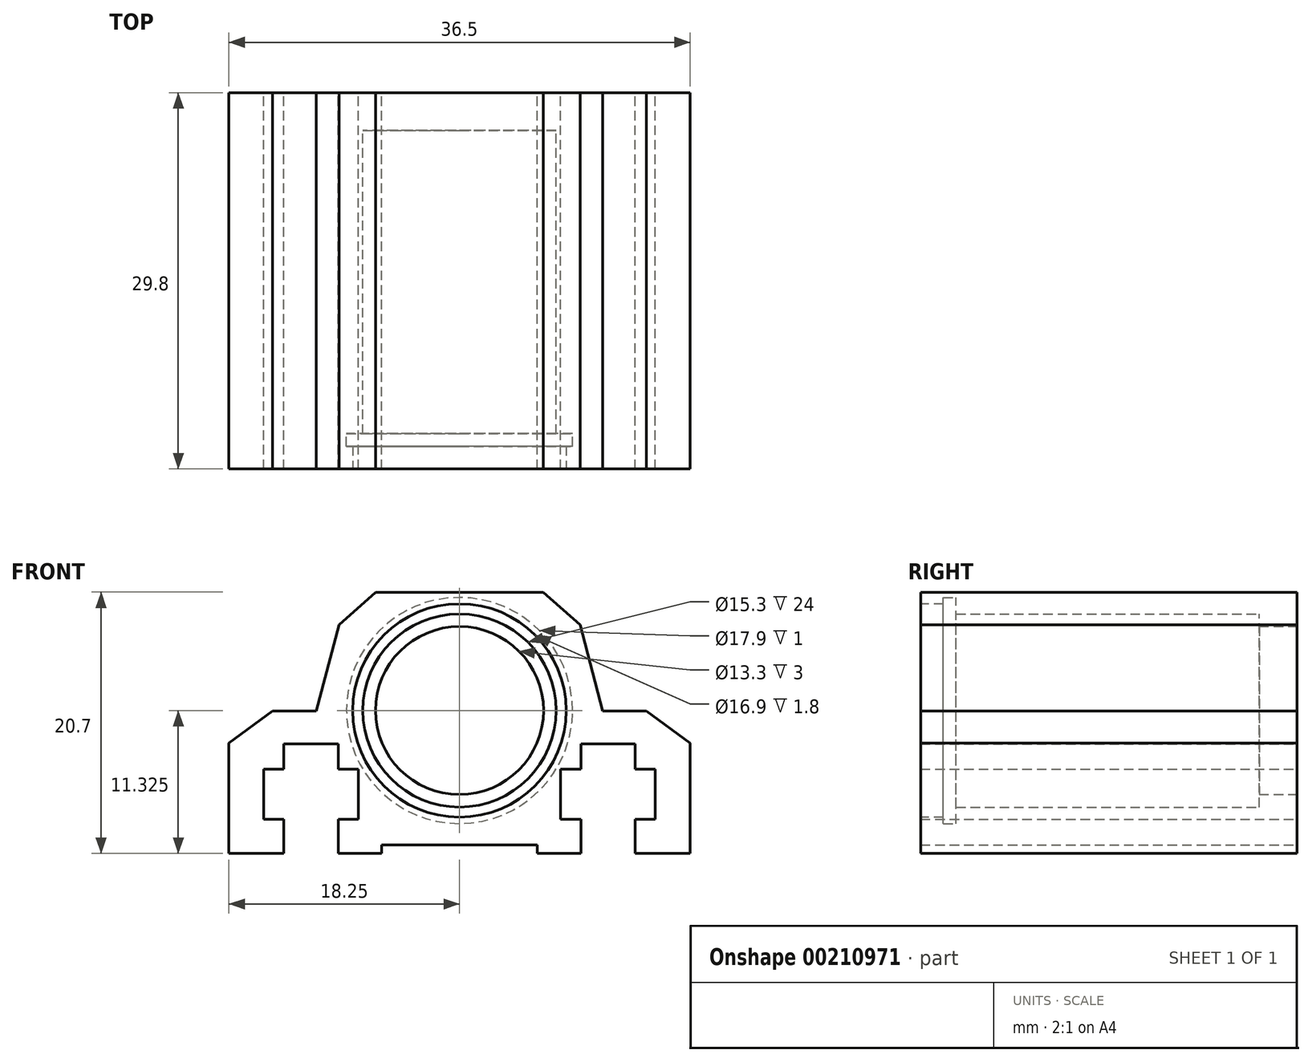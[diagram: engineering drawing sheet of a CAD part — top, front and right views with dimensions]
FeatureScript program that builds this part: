
annotation { "Feature Type Name" : "Feature", "Feature Type Description" : "" }
export const myFeature = defineFeature(function(context is Context, id is Id, definition is map)
    precondition{}
    {
        {
            var Q0;
            Q0=qCreatedBy(makeId("Front.planeOp"),FACE);
            var sketch = newSketch(context, id + "F0", { "sketchPlane" : qUnion([Q0])});
            skLineSegment(sketch, "E0", {"start": v(0, 0) * mm, "end": v(0, 26.85) * mm, "construction": true});
            skLineSegment(sketch, "E1", {"start": v(6.16, 0) * mm, "end": v(9.6, 0) * mm});
            skLineSegment(sketch, "E2", {"start": v(9.6, 0) * mm, "end": v(9.6, 2.7) * mm});
            skLineSegment(sketch, "E3", {"start": v(9.6, 2.7) * mm, "end": v(8, 2.7) * mm});
            skLineSegment(sketch, "E4", {"start": v(8, 2.7) * mm, "end": v(8, 6.7) * mm});
            skLineSegment(sketch, "E5", {"start": v(8, 6.7) * mm, "end": v(9.6, 6.7) * mm});
            skLineSegment(sketch, "E6", {"start": v(15.5, 6.7) * mm, "end": v(15.5, 2.7) * mm});
            skLineSegment(sketch, "E7", {"start": v(15.5, 2.7) * mm, "end": v(13.9, 2.7) * mm});
            skLineSegment(sketch, "E8", {"start": v(13.9, 2.7) * mm, "end": v(13.9, 0) * mm});
            skLineSegment(sketch, "E9", {"start": v(13.9, 0) * mm, "end": v(18.25, 0) * mm});
            skLineSegment(sketch, "E10", {"start": v(18.25, 0) * mm, "end": v(18.25, 8.74) * mm});
            skLineSegment(sketch, "E11", {"start": v(14.8, 11.3) * mm, "end": v(11.33, 11.3) * mm});
            skLineSegment(sketch, "E12", {"start": v(13.9, 6.7) * mm, "end": v(13.9, 8.67) * mm});
            skLineSegment(sketch, "E13", {"start": v(13.9, 8.67) * mm, "end": v(9.6, 8.67) * mm});
            skLineSegment(sketch, "E14", {"start": v(9.6, 8.67) * mm, "end": v(9.6, 6.7) * mm});
            skLineSegment(sketch, "E15.trimOffspring", {"start": v(13.9, 6.7) * mm, "end": v(15.5, 6.7) * mm});
            skLineSegment(sketch, "E16", {"start": v(6.16, 0) * mm, "end": v(6.16, 0.68) * mm});
            skLineSegment(sketch, "E17", {"start": v(6.16, 0.68) * mm, "end": v(0, 0.68) * mm});
            skCircle(sketch, "E18", {"center": v(0, 11.33) * mm, "radius": 7.65 * mm});
            skLineSegment(sketch, "E19", {"start": v(11.33, 11.3) * mm, "end": v(9.54, 18.1) * mm});
            skLineSegment(sketch, "E20", {"start": v(6.64, 20.7) * mm, "end": v(0, 20.7) * mm});
            skLineSegment(sketch, "E21.MirrorCS", {"start": v(-13.9, 6.7) * mm, "end": v(-15.5, 6.7) * mm});
            skLineSegment(sketch, "E22.MirrorCS", {"start": v(-9.6, 8.67) * mm, "end": v(-9.6, 6.7) * mm});
            skLineSegment(sketch, "E23.MirrorCS", {"start": v(-6.16, 0) * mm, "end": v(-6.16, 0.68) * mm});
            skLineSegment(sketch, "E24.MirrorCS", {"start": v(-13.9, 6.7) * mm, "end": v(-13.9, 8.67) * mm});
            skLineSegment(sketch, "E25.MirrorCS", {"start": v(-9.6, 2.7) * mm, "end": v(-8, 2.7) * mm});
            skLineSegment(sketch, "E26.MirrorCS", {"start": v(-15.5, 2.7) * mm, "end": v(-13.9, 2.7) * mm});
            skLineSegment(sketch, "E27.MirrorCS", {"start": v(-8, 6.7) * mm, "end": v(-9.6, 6.7) * mm});
            skLineSegment(sketch, "E28.MirrorCS", {"start": v(-6.16, 0) * mm, "end": v(-9.6, 0) * mm});
            skLineSegment(sketch, "E29.MirrorCS", {"start": v(-13.9, 8.67) * mm, "end": v(-9.6, 8.67) * mm});
            skLineSegment(sketch, "E30.MirrorCS", {"start": v(-9.6, 0) * mm, "end": v(-9.6, 2.7) * mm});
            skLineSegment(sketch, "E31.MirrorCS", {"start": v(-11.33, 11.3) * mm, "end": v(-9.54, 18.1) * mm});
            skLineSegment(sketch, "E32.MirrorCS", {"start": v(-18.25, 0) * mm, "end": v(-18.25, 8.74) * mm});
            skLineSegment(sketch, "E33.MirrorCS", {"start": v(-13.9, 0) * mm, "end": v(-18.25, 0) * mm});
            skLineSegment(sketch, "E34.MirrorCS", {"start": v(-6.64, 20.7) * mm, "end": v(0, 20.7) * mm});
            skLineSegment(sketch, "E35.MirrorCS", {"start": v(-14.8, 11.3) * mm, "end": v(-11.33, 11.3) * mm});
            skLineSegment(sketch, "E36.MirrorCS", {"start": v(-6.16, 0.68) * mm, "end": v(0, 0.68) * mm});
            skLineSegment(sketch, "E37.MirrorCS", {"start": v(-13.9, 2.7) * mm, "end": v(-13.9, 0) * mm});
            skLineSegment(sketch, "E38.MirrorCS", {"start": v(-8, 2.7) * mm, "end": v(-8, 6.7) * mm});
            skLineSegment(sketch, "E39.MirrorCS", {"start": v(-15.5, 6.7) * mm, "end": v(-15.5, 2.7) * mm});
            skLineSegment(sketch, "E40", {"start": v(18.25, 8.74) * mm, "end": v(14.8, 11.3) * mm});
            skLineSegment(sketch, "E41", {"start": v(9.54, 18.1) * mm, "end": v(6.64, 20.7) * mm});
            skPoint(sketch, "E42.orphan", {"position": v(8.85, 20.7) * mm});
            skPoint(sketch, "E43.orphan", {"position": v(18.25, 11.3) * mm});
            skLineSegment(sketch, "E44.MirrorCS", {"start": v(-9.54, 18.1) * mm, "end": v(-6.64, 20.7) * mm});
            skLineSegment(sketch, "E45.MirrorCS", {"start": v(-18.25, 8.74) * mm, "end": v(-14.8, 11.3) * mm});
            skPoint(sketch, "E46.orphan", {"position": v(-8.85, 20.7) * mm});
            skPoint(sketch, "E47.orphan", {"position": v(-18.25, 11.3) * mm});
            skSolve(sketch);
        }
        {
            var Q0;
            Q0=makeQuery(id+"F0.imprint","IMPRINT",FACE,{"disambiguationData":[TD([[makeQuery(id+"F0.imprint","IMPRINT",EDGE,{"derivedFrom":sQuery(id+"F0.wireOp",EDGE,"E1")}),1.0]])]});
            extrude(context, id + "F1", {"entities" : qUnion([Q0]), "endBound" : BoundingType.SYMMETRIC, "depth" : (23.8 + 6) * mm});
        }
        {
            var Q0;
            Q0=makeQuery(id+"F1.opExtrude","CAP_FACE",FACE,{"disambiguationData":[OSD([sQuery(id+"F0.wireOp",EDGE,"E1"),sQuery(id+"F0.wireOp",EDGE,"E2"),sQuery(id+"F0.wireOp",EDGE,"E3"),sQuery(id+"F0.wireOp",EDGE,"E4"),sQuery(id+"F0.wireOp",EDGE,"E5"),sQuery(id+"F0.wireOp",EDGE,"E6"),sQuery(id+"F0.wireOp",EDGE,"E7"),sQuery(id+"F0.wireOp",EDGE,"E8"),sQuery(id+"F0.wireOp",EDGE,"E9"),sQuery(id+"F0.wireOp",EDGE,"E10"),sQuery(id+"F0.wireOp",EDGE,"E11"),sQuery(id+"F0.wireOp",EDGE,"E12"),sQuery(id+"F0.wireOp",EDGE,"E13"),sQuery(id+"F0.wireOp",EDGE,"E14"),sQuery(id+"F0.wireOp",EDGE,"E15.trimOffspring"),sQuery(id+"F0.wireOp",EDGE,"E16"),sQuery(id+"F0.wireOp",EDGE,"E17"),sQuery(id+"F0.wireOp",EDGE,"E18"),sQuery(id+"F0.wireOp",EDGE,"E19"),sQuery(id+"F0.wireOp",EDGE,"E20"),sQuery(id+"F0.wireOp",EDGE,"E21.MirrorCS"),sQuery(id+"F0.wireOp",EDGE,"E22.MirrorCS"),sQuery(id+"F0.wireOp",EDGE,"E23.MirrorCS"),sQuery(id+"F0.wireOp",EDGE,"E24.MirrorCS"),sQuery(id+"F0.wireOp",EDGE,"E25.MirrorCS"),sQuery(id+"F0.wireOp",EDGE,"E26.MirrorCS"),sQuery(id+"F0.wireOp",EDGE,"E27.MirrorCS"),sQuery(id+"F0.wireOp",EDGE,"E28.MirrorCS"),sQuery(id+"F0.wireOp",EDGE,"E29.MirrorCS"),sQuery(id+"F0.wireOp",EDGE,"E30.MirrorCS"),sQuery(id+"F0.wireOp",EDGE,"E31.MirrorCS"),sQuery(id+"F0.wireOp",EDGE,"E32.MirrorCS"),sQuery(id+"F0.wireOp",EDGE,"E33.MirrorCS"),sQuery(id+"F0.wireOp",EDGE,"E34.MirrorCS"),sQuery(id+"F0.wireOp",EDGE,"E35.MirrorCS"),sQuery(id+"F0.wireOp",EDGE,"E36.MirrorCS"),sQuery(id+"F0.wireOp",EDGE,"E37.MirrorCS"),sQuery(id+"F0.wireOp",EDGE,"E38.MirrorCS"),sQuery(id+"F0.wireOp",EDGE,"E39.MirrorCS")])],"isStart":false});
            cPlane(context, id + "F2", {"entities" : qUnion([Q0]), "cplaneType" : CPlaneType.OFFSET, "offset" : (3 - 0.2) * mm, "oppositeDirection" : true, "width" : 150 * mm, "height" : 150 * mm});
        }
        {
            var Q0;
            Q0=qCreatedBy(id+"F2.planeOp",FACE);
            var sketch = newSketch(context, id + "F3", { "sketchPlane" : qUnion([Q0])});
            skCircle(sketch, "E48", {"center": v(0, 11.33) * mm, "radius": 8.95 * mm});
            skSolve(sketch);
        }
        {
            var Q0;
            Q0=makeQuery(id+"F3.imprint","IMPRINT",FACE,{"disambiguationData":[TD([[makeQuery(id+"F3.imprint","IMPRINT",EDGE,{"derivedFrom":sQuery(id+"F3.wireOp",EDGE,"E48")}),1.0]])]});
            var Q1;
            Q1=sQuery(id+"F3.wireOp",EDGE,"E48");
            extrude(context, id + "F4", {"entities" : qUnion([Q0]), "operationType" : NewBodyOperationType.REMOVE, "surfaceEntities" : qUnion([Q1]), "depth" : 1 * mm});
        }
        {
            var Q0;
            Q0=makeQuery(id+"F1.opExtrude","CAP_FACE",FACE,{"disambiguationData":[OSD([sQuery(id+"F0.wireOp",EDGE,"E1"),sQuery(id+"F0.wireOp",EDGE,"E2"),sQuery(id+"F0.wireOp",EDGE,"E3"),sQuery(id+"F0.wireOp",EDGE,"E4"),sQuery(id+"F0.wireOp",EDGE,"E5"),sQuery(id+"F0.wireOp",EDGE,"E6"),sQuery(id+"F0.wireOp",EDGE,"E7"),sQuery(id+"F0.wireOp",EDGE,"E8"),sQuery(id+"F0.wireOp",EDGE,"E9"),sQuery(id+"F0.wireOp",EDGE,"E10"),sQuery(id+"F0.wireOp",EDGE,"E11"),sQuery(id+"F0.wireOp",EDGE,"E12"),sQuery(id+"F0.wireOp",EDGE,"E13"),sQuery(id+"F0.wireOp",EDGE,"E14"),sQuery(id+"F0.wireOp",EDGE,"E15.trimOffspring"),sQuery(id+"F0.wireOp",EDGE,"E16"),sQuery(id+"F0.wireOp",EDGE,"E17"),sQuery(id+"F0.wireOp",EDGE,"E18"),sQuery(id+"F0.wireOp",EDGE,"E19"),sQuery(id+"F0.wireOp",EDGE,"E20"),sQuery(id+"F0.wireOp",EDGE,"E21.MirrorCS"),sQuery(id+"F0.wireOp",EDGE,"E22.MirrorCS"),sQuery(id+"F0.wireOp",EDGE,"E23.MirrorCS"),sQuery(id+"F0.wireOp",EDGE,"E24.MirrorCS"),sQuery(id+"F0.wireOp",EDGE,"E25.MirrorCS"),sQuery(id+"F0.wireOp",EDGE,"E26.MirrorCS"),sQuery(id+"F0.wireOp",EDGE,"E27.MirrorCS"),sQuery(id+"F0.wireOp",EDGE,"E28.MirrorCS"),sQuery(id+"F0.wireOp",EDGE,"E29.MirrorCS"),sQuery(id+"F0.wireOp",EDGE,"E30.MirrorCS"),sQuery(id+"F0.wireOp",EDGE,"E31.MirrorCS"),sQuery(id+"F0.wireOp",EDGE,"E32.MirrorCS"),sQuery(id+"F0.wireOp",EDGE,"E33.MirrorCS"),sQuery(id+"F0.wireOp",EDGE,"E34.MirrorCS"),sQuery(id+"F0.wireOp",EDGE,"E35.MirrorCS"),sQuery(id+"F0.wireOp",EDGE,"E36.MirrorCS"),sQuery(id+"F0.wireOp",EDGE,"E37.MirrorCS"),sQuery(id+"F0.wireOp",EDGE,"E38.MirrorCS"),sQuery(id+"F0.wireOp",EDGE,"E39.MirrorCS")])],"isStart":true});
            var sketch = newSketch(context, id + "F5", { "sketchPlane" : qUnion([Q0])});
            skCircle(sketch, "E49", {"center": v(0, 11.33) * mm, "radius": 6.65 * mm});
            skSolve(sketch);
        }
        {
            var Q0;
            Q0=makeQuery(id+"F5.imprint","IMPRINT",FACE,{"disambiguationData":[TD([[makeQuery(id+"F5.imprint","IMPRINT",EDGE,{"derivedFrom":sQuery(id+"F5.wireOp",EDGE,"E49")}),-1.0]])]});
            extrude(context, id + "F6", {"entities" : qUnion([Q0]), "operationType" : NewBodyOperationType.ADD, "oppositeDirection" : true, "depth" : 3 * mm});
        }
        {
            var Q0;
            Q0=makeQuery(id+"F1.opExtrude","CAP_FACE",FACE,{"disambiguationData":[OSD([sQuery(id+"F0.wireOp",EDGE,"E1"),sQuery(id+"F0.wireOp",EDGE,"E2"),sQuery(id+"F0.wireOp",EDGE,"E3"),sQuery(id+"F0.wireOp",EDGE,"E4"),sQuery(id+"F0.wireOp",EDGE,"E5"),sQuery(id+"F0.wireOp",EDGE,"E6"),sQuery(id+"F0.wireOp",EDGE,"E7"),sQuery(id+"F0.wireOp",EDGE,"E8"),sQuery(id+"F0.wireOp",EDGE,"E9"),sQuery(id+"F0.wireOp",EDGE,"E10"),sQuery(id+"F0.wireOp",EDGE,"E11"),sQuery(id+"F0.wireOp",EDGE,"E12"),sQuery(id+"F0.wireOp",EDGE,"E13"),sQuery(id+"F0.wireOp",EDGE,"E14"),sQuery(id+"F0.wireOp",EDGE,"E15.trimOffspring"),sQuery(id+"F0.wireOp",EDGE,"E16"),sQuery(id+"F0.wireOp",EDGE,"E17"),sQuery(id+"F0.wireOp",EDGE,"E18"),sQuery(id+"F0.wireOp",EDGE,"E19"),sQuery(id+"F0.wireOp",EDGE,"E20"),sQuery(id+"F0.wireOp",EDGE,"E21.MirrorCS"),sQuery(id+"F0.wireOp",EDGE,"E22.MirrorCS"),sQuery(id+"F0.wireOp",EDGE,"E23.MirrorCS"),sQuery(id+"F0.wireOp",EDGE,"E24.MirrorCS"),sQuery(id+"F0.wireOp",EDGE,"E25.MirrorCS"),sQuery(id+"F0.wireOp",EDGE,"E26.MirrorCS"),sQuery(id+"F0.wireOp",EDGE,"E27.MirrorCS"),sQuery(id+"F0.wireOp",EDGE,"E28.MirrorCS"),sQuery(id+"F0.wireOp",EDGE,"E29.MirrorCS"),sQuery(id+"F0.wireOp",EDGE,"E30.MirrorCS"),sQuery(id+"F0.wireOp",EDGE,"E31.MirrorCS"),sQuery(id+"F0.wireOp",EDGE,"E32.MirrorCS"),sQuery(id+"F0.wireOp",EDGE,"E33.MirrorCS"),sQuery(id+"F0.wireOp",EDGE,"E34.MirrorCS"),sQuery(id+"F0.wireOp",EDGE,"E35.MirrorCS"),sQuery(id+"F0.wireOp",EDGE,"E36.MirrorCS"),sQuery(id+"F0.wireOp",EDGE,"E37.MirrorCS"),sQuery(id+"F0.wireOp",EDGE,"E38.MirrorCS"),sQuery(id+"F0.wireOp",EDGE,"E39.MirrorCS"),sQuery(id+"F0.wireOp",EDGE,"E40"),sQuery(id+"F0.wireOp",EDGE,"E41"),sQuery(id+"F0.wireOp",EDGE,"E44.MirrorCS"),sQuery(id+"F0.wireOp",EDGE,"E45.MirrorCS")])],"isStart":false});
            var sketch = newSketch(context, id + "F7", { "sketchPlane" : qUnion([Q0])});
            skCircle(sketch, "E50", {"center": v(0, 11.33) * mm, "radius": 8.45 * mm});
            skSolve(sketch);
        }
        {
            var Q0;
            Q0=qSketchRegion(id+"F7",true);
            var Q1;
            Q1=makeQuery(id+"F4.boolean.opBoolean","COPY",FACE,{"derivedFrom":makeQuery(id+"F4.opExtrude","CAP_FACE",FACE,{"disambiguationData":[OSD([sQuery(id+"F3.wireOp",EDGE,"E48")])],"isStart":true})});
            extrude(context, id + "F8", {"entities" : qUnion([Q0]), "operationType" : NewBodyOperationType.REMOVE, "endBound" : BoundingType.UP_TO_SURFACE, "oppositeDirection" : true, "endBoundEntityFace" : qUnion([Q1]), "depth" : 3 * mm});
        }
    });
